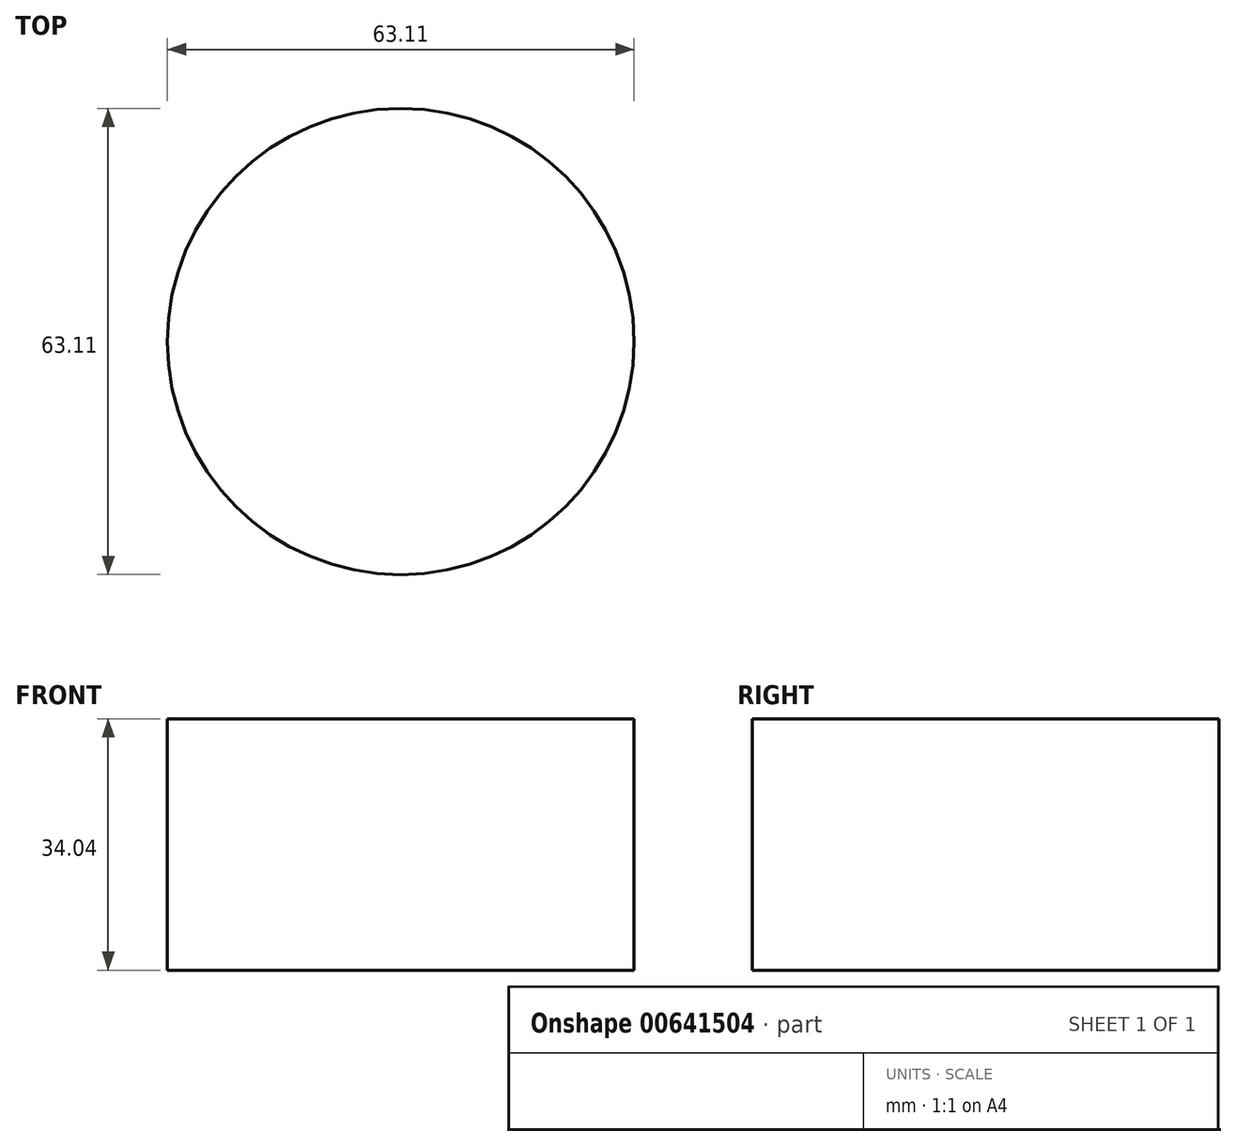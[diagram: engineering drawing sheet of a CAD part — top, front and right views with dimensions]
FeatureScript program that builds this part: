
annotation { "Feature Type Name" : "Feature", "Feature Type Description" : "" }
export const myFeature = defineFeature(function(context is Context, id is Id, definition is map)
    precondition{}
    {
        {
            var Q0;
            Q0=qCreatedBy(makeId("Top.planeOp"),FACE);
            var sketch = newSketch(context, id + "F0", { "sketchPlane" : qUnion([Q0])});
            skCircle(sketch, "E0", {"center": v(-66.35, -44.03) * mm, "radius": 31.56 * mm});
            skSolve(sketch);
        }
        {
            var Q0;
            Q0 = qSketchRegion(id + "F0", true);
            extrude(context, id + "F1", {"entities" : qUnion([Q0]), "depth" : 34.04 * mm, "offsetDistance" : 25.4 * mm});
        }
    });
